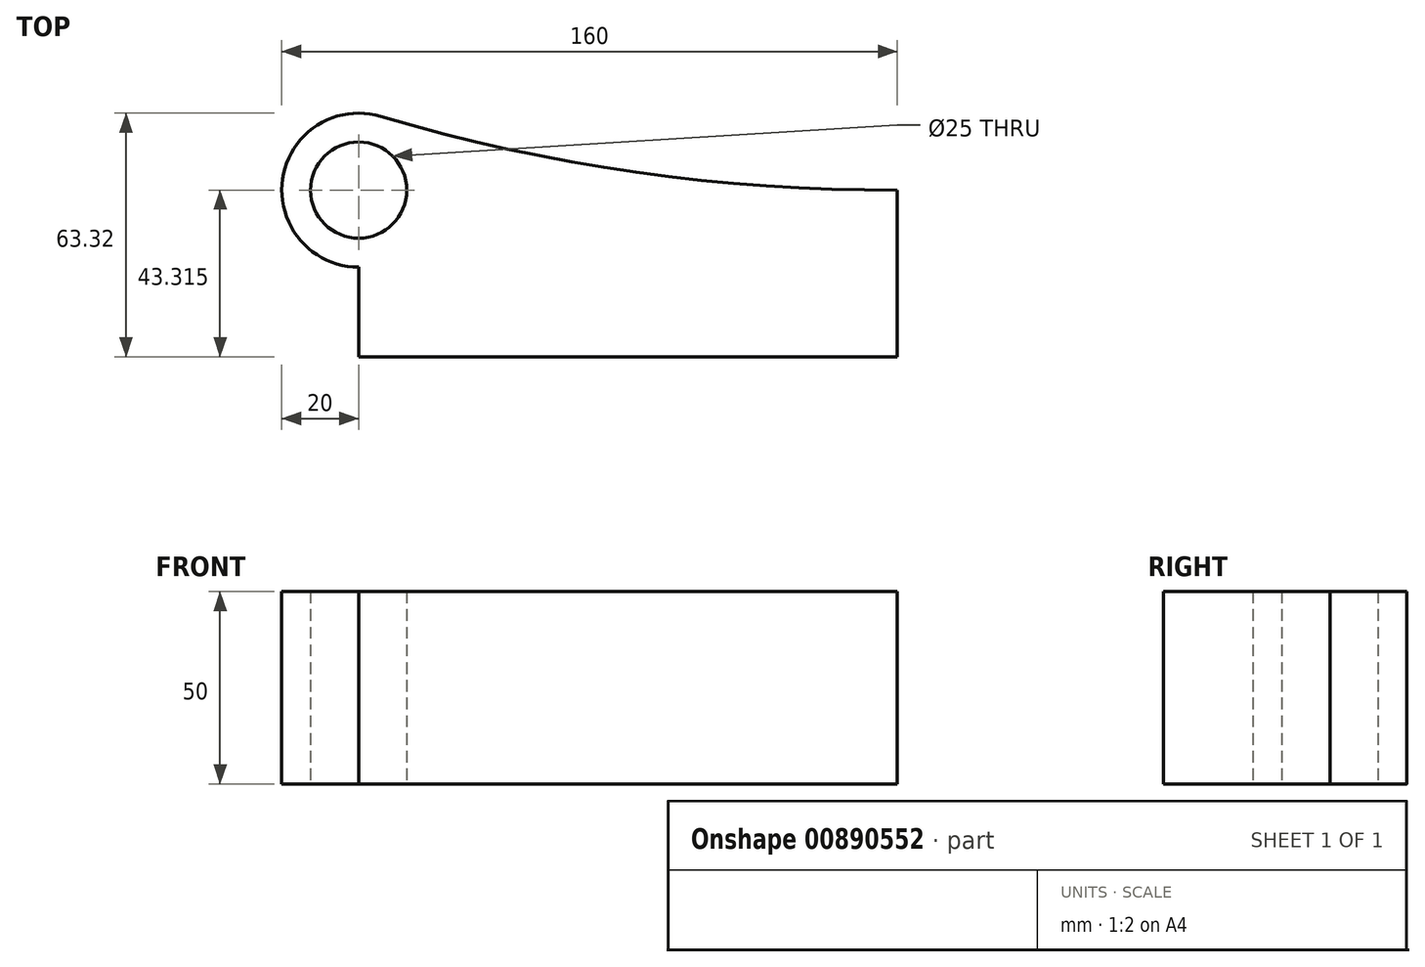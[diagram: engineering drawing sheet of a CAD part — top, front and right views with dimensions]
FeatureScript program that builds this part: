
annotation { "Feature Type Name" : "Feature", "Feature Type Description" : "" }
export const myFeature = defineFeature(function(context is Context, id is Id, definition is map)
    precondition{}
    {
        {
            var Q0;
            Q0=qCreatedBy(makeId("Top.planeOp"),FACE);
            var sketch = newSketch(context, id + "F0", { "sketchPlane" : qUnion([Q0])});
            skLineSegment(sketch, "E0.left", {"start": v(426.95, -28.81) * mm, "end": v(426.95, 80.25) * mm});
            skLineSegment(sketch, "E1.bottom", {"start": v(-70, 21.66) * mm, "end": v(70, 21.66) * mm});
            skLineSegment(sketch, "E1.top", {"start": v(-70, -21.66) * mm, "end": v(70, -21.66) * mm});
            skLineSegment(sketch, "E1.left", {"start": v(-70, 21.66) * mm, "end": v(-70, -21.66) * mm});
            skLineSegment(sketch, "E1.right", {"start": v(70, 21.66) * mm, "end": v(70, -21.66) * mm});
            skPoint(sketch, "E1.middle", {"position": v(0, 0) * mm});
            skCircle(sketch, "E2", {"center": v(-70, 21.66) * mm, "radius": 20 * mm});
            skArc(sketch, "E3", {"start": v(-64.3, 40.82) * mm, "mid": v(2.14, 26.28) * mm, "end": v(70, 21.66) * mm});
            skCircle(sketch, "E4", {"center": v(-70, 21.66) * mm, "radius": 12.5 * mm});
            skSolve(sketch);
        }
        {
            var Q0;
            {var subQ4=sQuery(id+"F0.wireOp",EDGE,"E1.bottom");var subQ6=sQuery(id+"F0.wireOp",EDGE,"E4");var subQ8=makeQuery(id+"F0.imprint","INTERSECT",VERTEX,{"derivedFrom":[subQ4,subQ6]});Q0=makeQuery(id+"F0.imprint","IMPRINT",FACE,{"disambiguationData":[TD([[makeQuery(id+"F0.imprint","IMPRINT",EDGE,{"disambiguationData":[TD([[subQ8,-1.0]])],"derivedFrom":subQ4}),1.0]])]});}
            var Q1;
            {var subQ1=sQuery(id+"F0.wireOp",EDGE,"E1.top");Q1=makeQuery(id+"F0.imprint","IMPRINT",FACE,{"disambiguationData":[TD([[makeQuery(id+"F0.imprint","IMPRINT",EDGE,{"derivedFrom":subQ1}),1.0]])]});}
            var Q2;
            {var subQ0=sQuery(id+"F0.wireOp",EDGE,"E4");var subQ1=sQuery(id+"F0.wireOp",EDGE,"E1.bottom");var subQ2=makeQuery(id+"F0.imprint","INTERSECT",VERTEX,{"derivedFrom":[subQ1,subQ0]});Q2=makeQuery(id+"F0.imprint","IMPRINT",FACE,{"disambiguationData":[TD([[makeQuery(id+"F0.imprint","IMPRINT",EDGE,{"disambiguationData":[TD([[subQ2,-1.0]])],"derivedFrom":subQ1}),-1.0]])]});}
            var Q3;
            {var subQ0=sQuery(id+"F0.wireOp",EDGE,"E3");var subQ1=sQuery(id+"F0.wireOp",EDGE,"E1.bottom");var subQ2=makeQuery(id+"F0.imprint","INTERSECT",VERTEX,{"derivedFrom":[subQ1,subQ0]});Q3=makeQuery(id+"F0.imprint","IMPRINT",FACE,{"disambiguationData":[TD([[makeQuery(id+"F0.imprint","IMPRINT",EDGE,{"disambiguationData":[TD([[subQ2,1.0]])],"derivedFrom":subQ1}),1.0]])]});}
            extrude(context, id + "F1", {"entities" : qUnion([Q0, Q1, Q2, Q3]), "depth" : 50 * mm, "offsetDistance" : 25 * mm});
        }
    });
